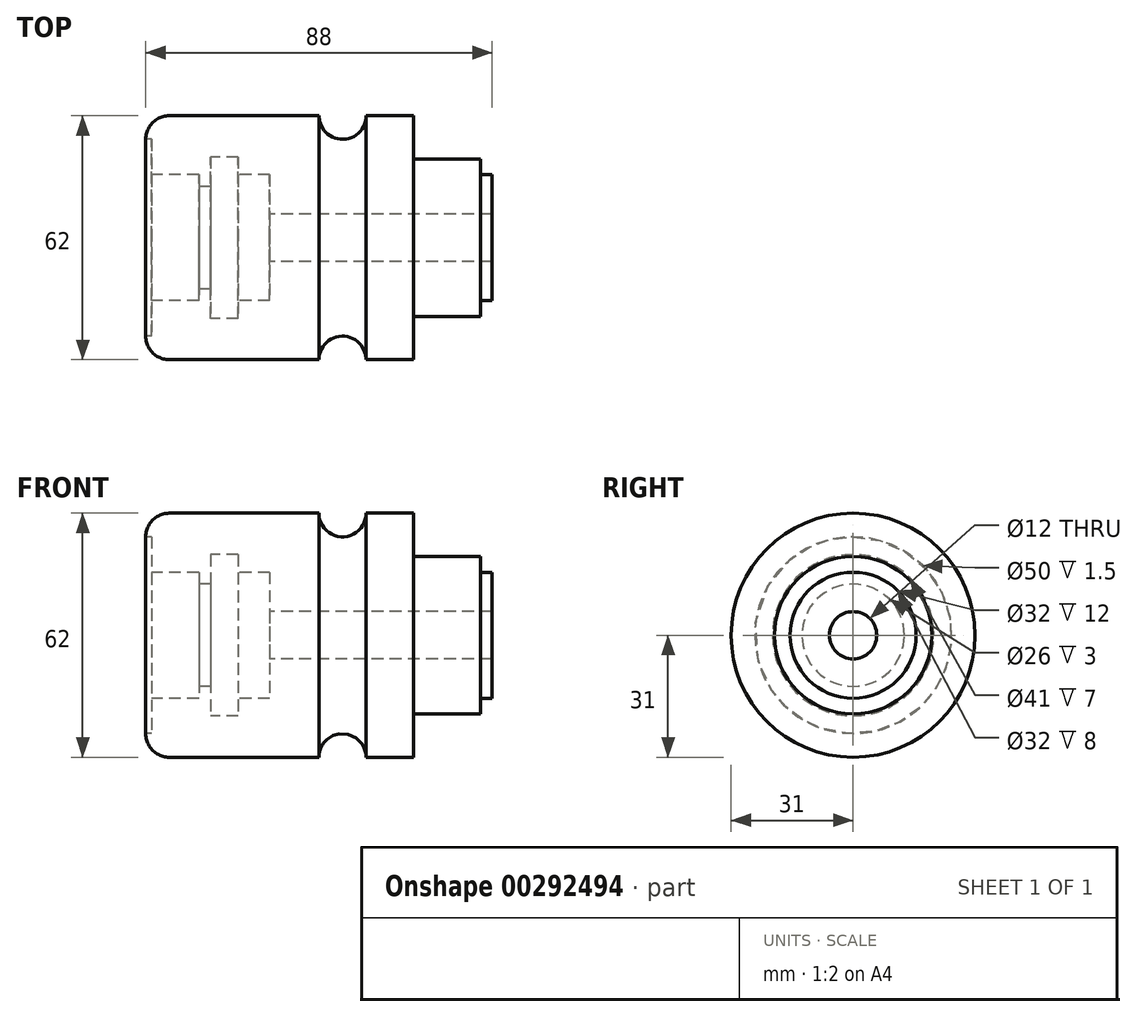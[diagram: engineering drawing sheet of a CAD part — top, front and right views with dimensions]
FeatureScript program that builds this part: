
annotation { "Feature Type Name" : "Feature", "Feature Type Description" : "" }
export const myFeature = defineFeature(function(context is Context, id is Id, definition is map)
    precondition{}
    {
        {
            var Q0;
            Q0=qCreatedBy(makeId("Front.planeOp"),FACE);
            var sketch = newSketch(context, id + "F0", { "sketchPlane" : qUnion([Q0])});
            skLineSegment(sketch, "E0", {"start": v(0, 0) * mm, "end": v(0, 16) * mm});
            skLineSegment(sketch, "E1", {"start": v(0, 16) * mm, "end": v(-3, 16) * mm});
            skLineSegment(sketch, "E2", {"start": v(-3, 16) * mm, "end": v(-3, 20) * mm});
            skLineSegment(sketch, "E3", {"start": v(-3, 20) * mm, "end": v(-20, 20) * mm});
            skLineSegment(sketch, "E4", {"start": v(-20, 20) * mm, "end": v(-20, 31) * mm});
            skLineSegment(sketch, "E5", {"start": v(-20, 31) * mm, "end": v(-32, 31) * mm});
            skLineSegment(sketch, "E6", {"start": v(-88, 25) * mm, "end": v(-88, 0) * mm});
            skLineSegment(sketch, "E7", {"start": v(-88, 0) * mm, "end": v(0, 0) * mm});
            skPoint(sketch, "E8.visualSharp", {"position": v(-88, 31) * mm});
            skArc(sketch, "E8.filletArc", {"start": v(-82, 31) * mm, "mid": v(-86.24, 29.24) * mm, "end": v(-88, 25) * mm});
            skArc(sketch, "E9", {"start": v(-44, 31) * mm, "mid": v(-38, 25) * mm, "end": v(-32, 31) * mm});
            skLineSegment(sketch, "E10.trimOffspring", {"start": v(-44, 31) * mm, "end": v(-82, 31) * mm});
            skLineSegment(sketch, "E11", {"start": v(-88, 0) * mm, "end": v(-88, 25) * mm});
            skLineSegment(sketch, "E12", {"start": v(-88, 25) * mm, "end": v(-86.5, 25) * mm});
            skLineSegment(sketch, "E13", {"start": v(-86.5, 25) * mm, "end": v(-86.5, 16) * mm});
            skLineSegment(sketch, "E14", {"start": v(-86.5, 16) * mm, "end": v(-74.5, 16) * mm});
            skLineSegment(sketch, "E15", {"start": v(-74.5, 16) * mm, "end": v(-74.5, 13) * mm});
            skLineSegment(sketch, "E16", {"start": v(-74.5, 13) * mm, "end": v(-71.5, 13) * mm});
            skLineSegment(sketch, "E17", {"start": v(-71.5, 13) * mm, "end": v(-71.5, 20.5) * mm});
            skLineSegment(sketch, "E18", {"start": v(-71.5, 20.5) * mm, "end": v(-64.5, 20.5) * mm});
            skLineSegment(sketch, "E19", {"start": v(-64.5, 20.5) * mm, "end": v(-64.5, 16) * mm});
            skLineSegment(sketch, "E20", {"start": v(-64.5, 16) * mm, "end": v(-56.5, 16) * mm});
            skLineSegment(sketch, "E21", {"start": v(-56.5, 16) * mm, "end": v(-56.5, 6) * mm});
            skLineSegment(sketch, "E22", {"start": v(-56.5, 6) * mm, "end": v(0, 6) * mm});
            skSolve(sketch);
        }
        {
            var Q0;
            {var subQ0=sQuery(id+"F0.wireOp",EDGE,"E1");Q0=makeQuery(id+"F0.imprint","IMPRINT",FACE,{"disambiguationData":[TD([[makeQuery(id+"F0.imprint","IMPRINT",EDGE,{"derivedFrom":subQ0}),1.0]])]});}
            var Q1;
            Q1=sQuery(id+"F0.wireOp",EDGE,"E7");
            revolve(context, id + "F1", {"entities" : qUnion([Q0]), "axis" : qUnion([Q1]), "revolveType" : RevolveType.FULL});
        }
    });
